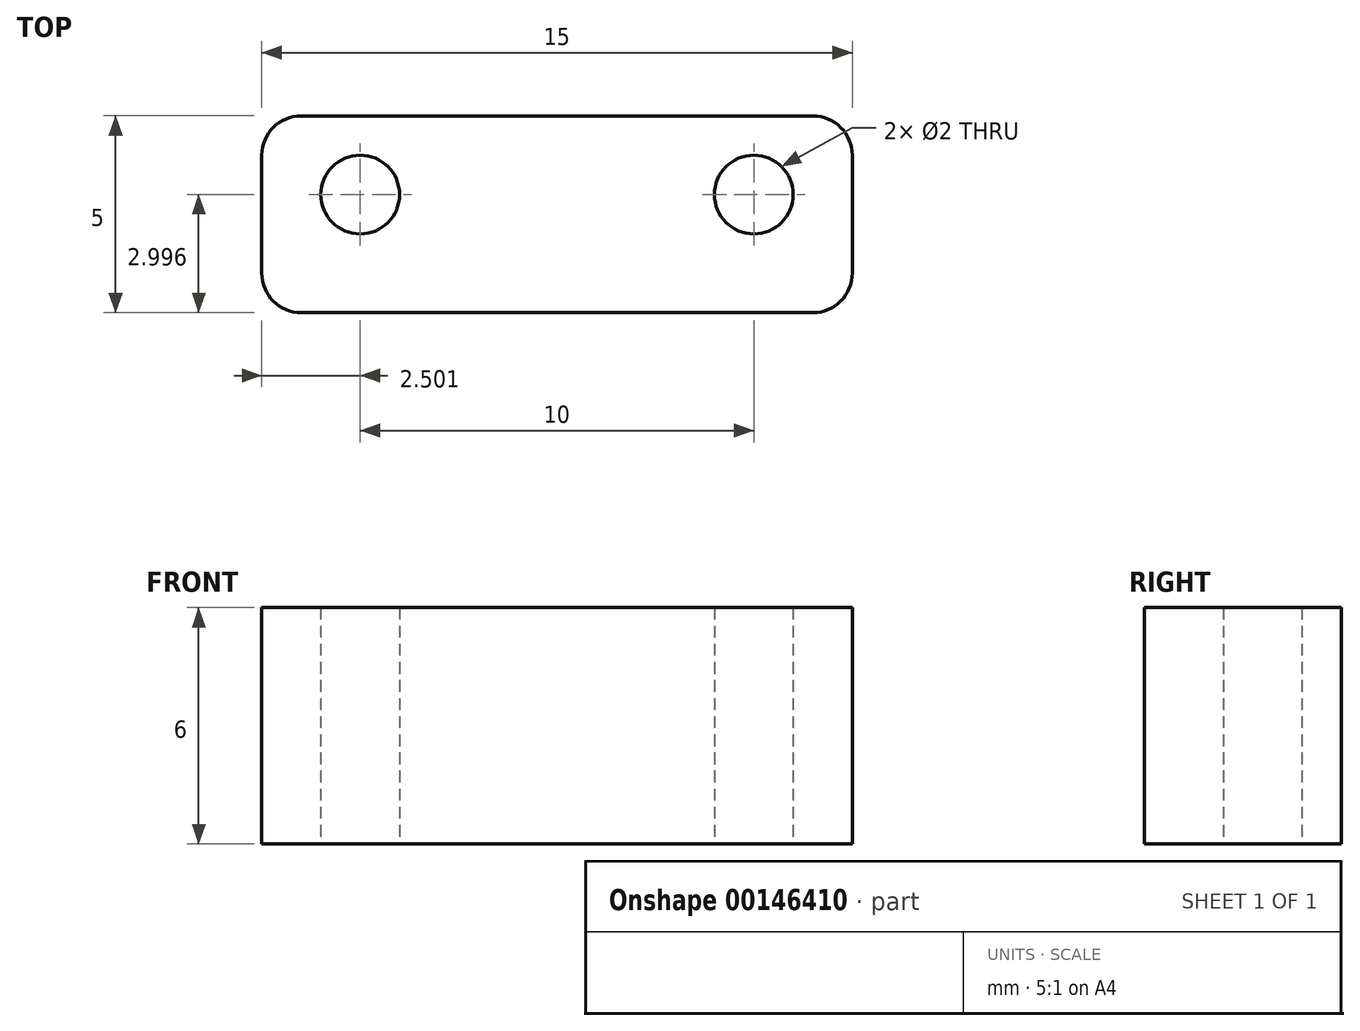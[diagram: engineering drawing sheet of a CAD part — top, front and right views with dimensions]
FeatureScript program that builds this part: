
annotation { "Feature Type Name" : "Feature", "Feature Type Description" : "" }
export const myFeature = defineFeature(function(context is Context, id is Id, definition is map)
    precondition{}
    {
        {
            var Q0;
            Q0=qCreatedBy(makeId("Top.planeOp"),FACE);
            var sketch = newSketch(context, id + "F0", { "sketchPlane" : qUnion([Q0])});
            skLineSegment(sketch, "E0.bottom", {"start": v(-7.6, -2.3) * mm, "end": v(7.4, -2.3) * mm});
            skLineSegment(sketch, "E0.top", {"start": v(-7.6, -7.3) * mm, "end": v(7.4, -7.3) * mm});
            skLineSegment(sketch, "E0.left", {"start": v(-7.6, -2.3) * mm, "end": v(-7.6, -7.3) * mm});
            skLineSegment(sketch, "E0.right", {"start": v(7.4, -2.3) * mm, "end": v(7.4, -7.3) * mm});
            skCircle(sketch, "E1", {"center": v(-5.1, -4.3) * mm, "radius": 1 * mm});
            skCircle(sketch, "E2", {"center": v(4.9, -4.3) * mm, "radius": 1 * mm});
            skSolve(sketch);
        }
        {
            var Q0;
            Q0=makeQuery(id+"F0.imprint","IMPRINT",FACE,{"disambiguationData":[TD([[makeQuery(id+"F0.imprint","IMPRINT",EDGE,{"derivedFrom":sQuery(id+"F0.wireOp",EDGE,"E0.bottom")}),-1.0]])]});
            extrude(context, id + "F1", {"entities" : qUnion([Q0]), "depth" : 6 * mm});
        }
        {
            var Q0;
            Q0=makeQuery(id+"F1.opExtrude","SWEPT_EDGE",EDGE,{"disambiguationData":[OSD([sQuery(id+"F0.wireOp",EDGE,"E0.top"),sQuery(id+"F0.wireOp",EDGE,"E0.left")])]});
            var Q1;
            Q1=makeQuery(id+"F1.opExtrude","SWEPT_EDGE",EDGE,{"disambiguationData":[OSD([sQuery(id+"F0.wireOp",EDGE,"E0.bottom"),sQuery(id+"F0.wireOp",EDGE,"E0.left")])]});
            var Q2;
            Q2=makeQuery(id+"F1.opExtrude","SWEPT_EDGE",EDGE,{"disambiguationData":[OSD([sQuery(id+"F0.wireOp",EDGE,"E0.top"),sQuery(id+"F0.wireOp",EDGE,"E0.right")])]});
            var Q3;
            Q3=makeQuery(id+"F1.opExtrude","SWEPT_EDGE",EDGE,{"disambiguationData":[OSD([sQuery(id+"F0.wireOp",EDGE,"E0.bottom"),sQuery(id+"F0.wireOp",EDGE,"E0.right")])]});
            fillet(context, id + "F2", {"entities" : qUnion([Q0, Q1, Q2, Q3]), "radius" : 1 * mm, "tangentPropagation" : true, "allowEdgeOverflow" : false});
        }
    });
